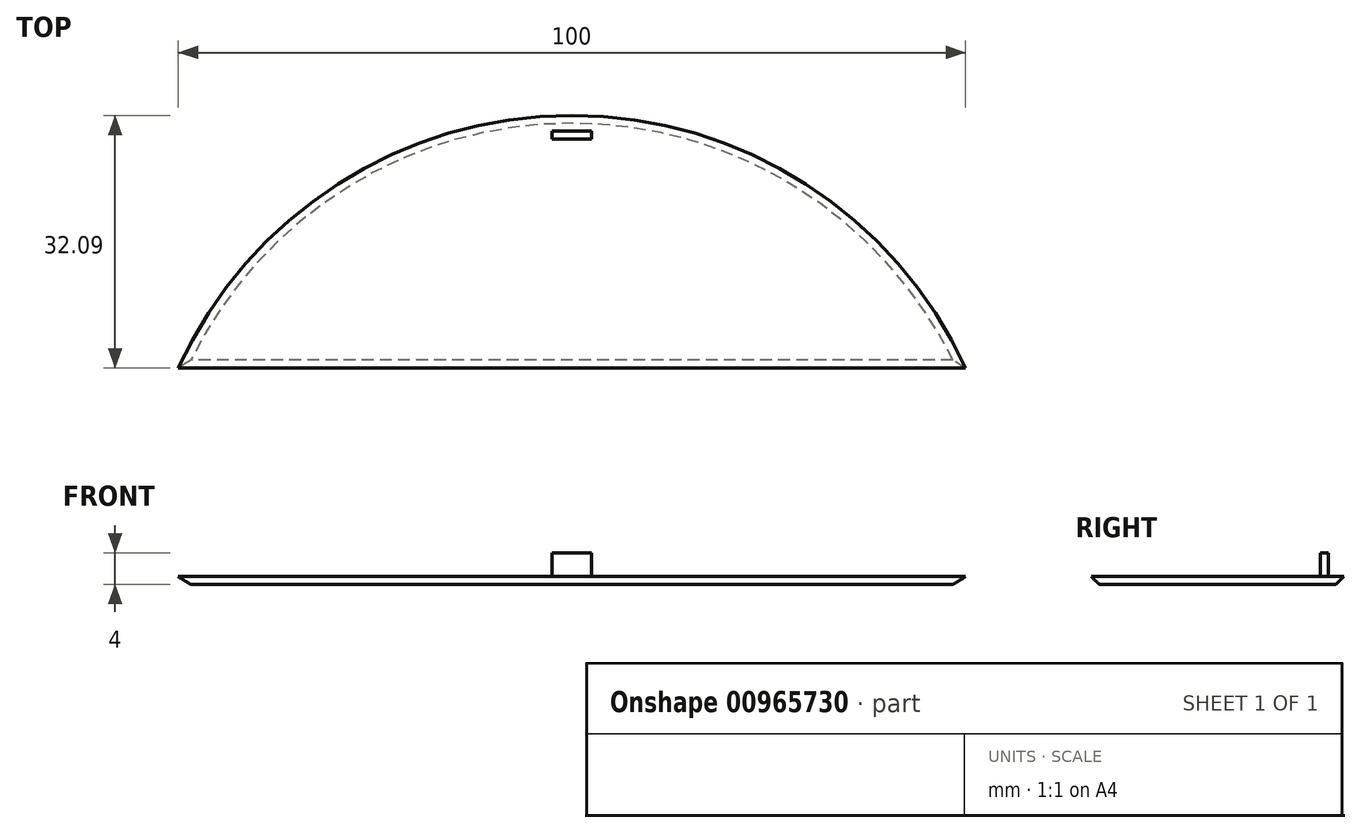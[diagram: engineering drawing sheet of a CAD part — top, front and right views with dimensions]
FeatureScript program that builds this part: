
annotation { "Feature Type Name" : "Feature", "Feature Type Description" : "" }
export const myFeature = defineFeature(function(context is Context, id is Id, definition is map)
    precondition{}
    {
        {
            var Q0;
            Q0=qCreatedBy(makeId("Top.planeOp"),FACE);
            var sketch = newSketch(context, id + "F0", { "sketchPlane" : qUnion([Q0])});
            skArc(sketch, "E0", {"start": v(50, 0) * mm, "mid": v(0, 32.09) * mm, "end": v(-50, 0) * mm});
            skLineSegment(sketch, "E1.bottom", {"start": v(2.5, 29.09) * mm, "end": v(-2.5, 29.09) * mm});
            skLineSegment(sketch, "E1.top", {"start": v(2.5, 30.09) * mm, "end": v(-2.5, 30.09) * mm});
            skLineSegment(sketch, "E1.left", {"start": v(2.5, 29.09) * mm, "end": v(2.5, 30.09) * mm});
            skLineSegment(sketch, "E1.right", {"start": v(-2.5, 29.09) * mm, "end": v(-2.5, 30.09) * mm});
            skPoint(sketch, "E1.middle", {"position": v(0, 29.59) * mm});
            skLineSegment(sketch, "E2", {"start": v(-50, 0) * mm, "end": v(50, 0) * mm});
            skSolve(sketch);
        }
        {
            var Q0;
            Q0=makeQuery(id+"F0.imprint","IMPRINT",FACE,{"disambiguationData":[TD([[makeQuery(id+"F0.imprint","IMPRINT",EDGE,{"derivedFrom":sQuery(id+"F0.wireOp",EDGE,"E1.bottom")}),-1.0]])]});
            extrude(context, id + "F1", {"entities" : qUnion([Q0]), "depth" : 4 * mm, "offsetDistance" : 25 * mm});
        }
        {
            var Q0;
            Q0=makeQuery(id+"F0.imprint","IMPRINT",FACE,{"disambiguationData":[TD([[makeQuery(id+"F0.imprint","IMPRINT",EDGE,{"derivedFrom":sQuery(id+"F0.wireOp",EDGE,"E0")}),1.0]])]});
            extrude(context, id + "F2", {"entities" : qUnion([Q0]), "operationType" : NewBodyOperationType.ADD, "depth" : 1 * mm, "offsetDistance" : 25 * mm});
        }
        {
            var Q0;
            Q0=makeQuery(id+"F2.opExtrude","CAP_EDGE",EDGE,{"disambiguationData":[OSD([sQuery(id+"F0.wireOp",EDGE,"E0")])],"isStart":true});
            var Q1;
            Q1=makeQuery(id+"F2.opExtrude","CAP_EDGE",EDGE,{"disambiguationData":[OSD([sQuery(id+"F0.wireOp",EDGE,"E2")])],"isStart":true});
            chamfer(context, id + "F3", {"entities" : qUnion([Q0, Q1]), "width" : 1 * mm, "tangentPropagation" : true});
        }
    });
